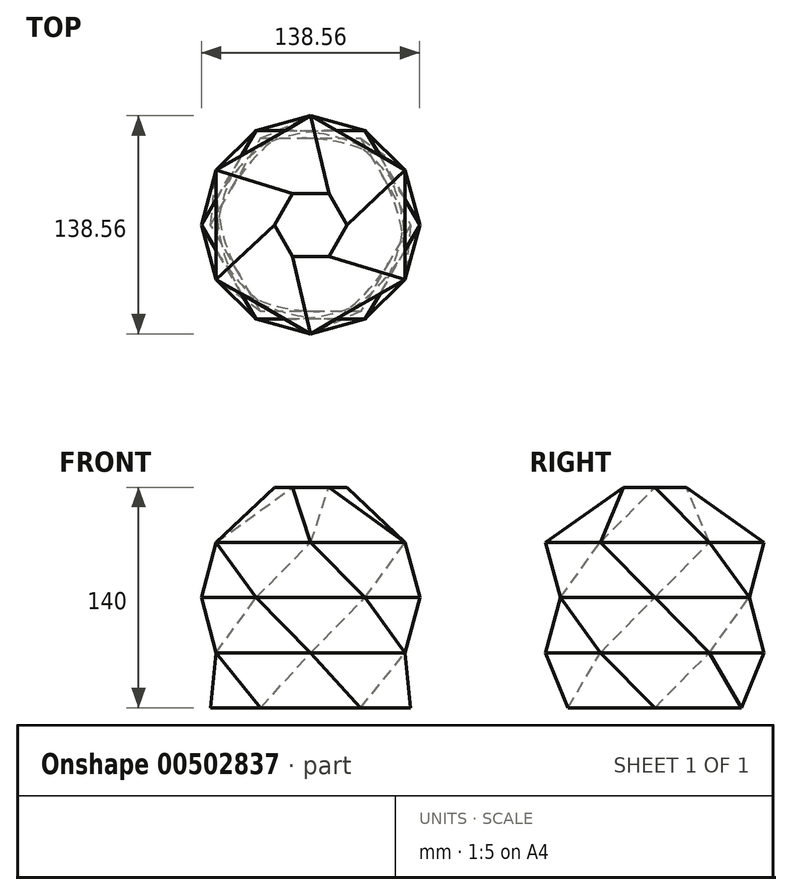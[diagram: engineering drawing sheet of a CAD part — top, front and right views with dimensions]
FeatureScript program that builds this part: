
annotation { "Feature Type Name" : "Feature", "Feature Type Description" : "" }
export const myFeature = defineFeature(function(context is Context, id is Id, definition is map)
    precondition{}
    {
        {
            var Q0;
            Q0=qCreatedBy(makeId("Top.planeOp"),FACE);
            cPlane(context, id + "F0", {"entities" : qUnion([Q0]), "cplaneType" : CPlaneType.OFFSET, "offset" : 35 * mm, "width" : 150 * mm, "height" : 150 * mm});
        }
        {
            var Q0;
            Q0=qCreatedBy(id+"F0.planeOp",FACE);
            cPlane(context, id + "F1", {"entities" : qUnion([Q0]), "cplaneType" : CPlaneType.OFFSET, "offset" : 35 * mm, "width" : 150 * mm, "height" : 150 * mm});
        }
        {
            var Q0;
            Q0=qCreatedBy(id+"F1.planeOp",FACE);
            cPlane(context, id + "F2", {"entities" : qUnion([Q0]), "cplaneType" : CPlaneType.OFFSET, "offset" : 35 * mm, "width" : 150 * mm, "height" : 150 * mm});
        }
        {
            var Q0;
            Q0=qCreatedBy(id+"F2.planeOp",FACE);
            cPlane(context, id + "F3", {"entities" : qUnion([Q0]), "cplaneType" : CPlaneType.OFFSET, "offset" : 35 * mm, "width" : 150 * mm, "height" : 150 * mm});
        }
        {
            var Q0;
            Q0=qCreatedBy(makeId("Top.planeOp"),FACE);
            var sketch = newSketch(context, id + "F4", { "sketchPlane" : qUnion([Q0])});
            skCircle(sketch, "E0.cCircle", {"center": v(0, 0) * mm, "radius": 55 * mm, "construction": true});
            skLineSegment(sketch, "E0.0", {"start": v(31.75, -55) * mm, "end": v(-31.75, -55) * mm});
            skLineSegment(sketch, "E0.1", {"start": v(-31.75, -55) * mm, "end": v(-63.5, 0) * mm});
            skLineSegment(sketch, "E0.2", {"start": v(-63.5, 0) * mm, "end": v(-31.75, 55) * mm});
            skLineSegment(sketch, "E0.3", {"start": v(-31.75, 55) * mm, "end": v(31.75, 55) * mm});
            skLineSegment(sketch, "E0.4", {"start": v(31.75, 55) * mm, "end": v(63.5, 0) * mm});
            skLineSegment(sketch, "E0.5", {"start": v(63.5, 0) * mm, "end": v(31.75, -55) * mm});
            skPoint(sketch, "E0.0.midPoint", {"position": v(0, -55) * mm});
            skSolve(sketch);
        }
        {
            var Q0;
            Q0=qCreatedBy(id+"F0.planeOp",FACE);
            var sketch = newSketch(context, id + "F5", { "sketchPlane" : qUnion([Q0])});
            skCircle(sketch, "E1.cCircle", {"center": v(0, 0) * mm, "radius": 60 * mm, "construction": true});
            skLineSegment(sketch, "E1.0", {"start": v(60, 34.64) * mm, "end": v(60, -34.64) * mm});
            skLineSegment(sketch, "E1.1", {"start": v(60, -34.64) * mm, "end": v(0, -69.28) * mm});
            skLineSegment(sketch, "E1.2", {"start": v(0, -69.28) * mm, "end": v(-60, -34.64) * mm});
            skLineSegment(sketch, "E1.3", {"start": v(-60, -34.64) * mm, "end": v(-60, 34.64) * mm});
            skLineSegment(sketch, "E1.4", {"start": v(-60, 34.64) * mm, "end": v(0, 69.28) * mm});
            skLineSegment(sketch, "E1.5", {"start": v(0, 69.28) * mm, "end": v(60, 34.64) * mm});
            skPoint(sketch, "E1.0.midPoint", {"position": v(60, 0) * mm});
            skSolve(sketch);
        }
        {
            var Q0;
            Q0=qCreatedBy(id+"F1.planeOp",FACE);
            var sketch = newSketch(context, id + "F6", { "sketchPlane" : qUnion([Q0])});
            skCircle(sketch, "E2.cCircle", {"center": v(0, 0) * mm, "radius": 60 * mm, "construction": true});
            skLineSegment(sketch, "E2.0", {"start": v(69.28, 0) * mm, "end": v(34.64, -60) * mm});
            skLineSegment(sketch, "E2.1", {"start": v(34.64, -60) * mm, "end": v(-34.64, -60) * mm});
            skLineSegment(sketch, "E2.2", {"start": v(-34.64, -60) * mm, "end": v(-69.28, 0) * mm});
            skLineSegment(sketch, "E2.3", {"start": v(-69.28, 0) * mm, "end": v(-34.64, 60) * mm});
            skLineSegment(sketch, "E2.4", {"start": v(-34.64, 60) * mm, "end": v(34.64, 60) * mm});
            skLineSegment(sketch, "E2.5", {"start": v(34.64, 60) * mm, "end": v(69.28, 0) * mm});
            skPoint(sketch, "E2.0.midPoint", {"position": v(51.96, -30) * mm});
            skSolve(sketch);
        }
        {
            var Q0;
            Q0=qCreatedBy(id+"F2.planeOp",FACE);
            var sketch = newSketch(context, id + "F7", { "sketchPlane" : qUnion([Q0])});
            skCircle(sketch, "E3.cCircle", {"center": v(0, 0) * mm, "radius": 60 * mm, "construction": true});
            skLineSegment(sketch, "E3.0", {"start": v(60, -34.64) * mm, "end": v(0, -69.28) * mm});
            skLineSegment(sketch, "E3.1", {"start": v(0, -69.28) * mm, "end": v(-60, -34.64) * mm});
            skLineSegment(sketch, "E3.2", {"start": v(-60, -34.64) * mm, "end": v(-60, 34.64) * mm});
            skLineSegment(sketch, "E3.3", {"start": v(-60, 34.64) * mm, "end": v(0, 69.28) * mm});
            skLineSegment(sketch, "E3.4", {"start": v(0, 69.28) * mm, "end": v(60, 34.64) * mm});
            skLineSegment(sketch, "E3.5", {"start": v(60, 34.64) * mm, "end": v(60, -34.64) * mm});
            skPoint(sketch, "E3.0.midPoint", {"position": v(30, -51.96) * mm});
            skSolve(sketch);
        }
        {
            var Q0;
            Q0=qCreatedBy(id+"F3.planeOp",FACE);
            var sketch = newSketch(context, id + "F8", { "sketchPlane" : qUnion([Q0])});
            skCircle(sketch, "E4.cCircle", {"center": v(0, 0) * mm, "radius": 20 * mm, "construction": true});
            skLineSegment(sketch, "E4.0", {"start": v(23.1, 0) * mm, "end": v(11.55, -20) * mm});
            skLineSegment(sketch, "E4.1", {"start": v(11.55, -20) * mm, "end": v(-11.55, -20) * mm});
            skLineSegment(sketch, "E4.2", {"start": v(-11.55, -20) * mm, "end": v(-23.1, 0) * mm});
            skLineSegment(sketch, "E4.3", {"start": v(-23.1, 0) * mm, "end": v(-11.55, 20) * mm});
            skLineSegment(sketch, "E4.4", {"start": v(-11.55, 20) * mm, "end": v(11.55, 20) * mm});
            skLineSegment(sketch, "E4.5", {"start": v(11.55, 20) * mm, "end": v(23.1, 0) * mm});
            skPoint(sketch, "E4.0.midPoint", {"position": v(17.32, -10) * mm});
            skSolve(sketch);
        }
        {
            var Q0;
            Q0=makeQuery(id+"F4.imprint","IMPRINT",FACE,{"disambiguationData":[TD([[makeQuery(id+"F4.imprint","IMPRINT",EDGE,{"derivedFrom":sQuery(id+"F4.wireOp",EDGE,"E0.0")}),-1.0]])]});
            var Q1;
            Q1=makeQuery(id+"F5.imprint","IMPRINT",FACE,{"disambiguationData":[TD([[makeQuery(id+"F5.imprint","IMPRINT",EDGE,{"derivedFrom":sQuery(id+"F5.wireOp",EDGE,"E1.0")}),-1.0]])]});
            var Q2;
            Q2=sQuery(id+"F4.wireOp",VERTEX,"E0.2.start");
            var Q3;
            Q3=sQuery(id+"F5.wireOp",VERTEX,"E1.4.start");
            loft(context, id + "F9", {"sheetProfilesArray" : [{ "sheetProfileEntities" : qUnion([Q0]) }, { "sheetProfileEntities" : qUnion([Q1]) }], "matchConnections" : true, "connections" : [{ "connectionEntities" : qUnion([Q2, Q3]), "connectionEdgeQueries" : qUnion([]), "connectionEdgeParameters" : [] }]});
        }
        {
            var Q1;
            Q1 = qSketchRegion(id + "F5", true);
            var Q2;
            Q2 = qSketchRegion(id + "F6", true);
            var Q3;
            Q3=sQuery(id+"F5.wireOp",VERTEX,"E1.3.start");
            var Q4;
            Q4=sQuery(id+"F6.wireOp",VERTEX,"E2.3.start");
            loft(context, id + "F10", {"operationType" : NewBodyOperationType.ADD, "sheetProfilesArray" : [{ "sheetProfileEntities" : qUnion([Q1]) }, { "sheetProfileEntities" : qUnion([Q2]) }], "matchConnections" : true, "connections" : [{ "connectionEntities" : qUnion([Q3, Q4]), "connectionEdgeQueries" : qUnion([]), "connectionEdgeParameters" : [] }]});
        }
        {
            var Q1;
            Q1 = qSketchRegion(id + "F6", true);
            var Q2;
            Q2 = qSketchRegion(id + "F7", true);
            var Q3;
            Q3=sQuery(id+"F6.wireOp",VERTEX,"E2.3.start");
            var Q4;
            Q4=sQuery(id+"F7.wireOp",VERTEX,"E3.3.start");
            loft(context, id + "F11", {"operationType" : NewBodyOperationType.ADD, "sheetProfilesArray" : [{ "sheetProfileEntities" : qUnion([Q1]) }, { "sheetProfileEntities" : qUnion([Q2]) }], "matchConnections" : true, "connections" : [{ "connectionEntities" : qUnion([Q3, Q4]), "connectionEdgeQueries" : qUnion([]), "connectionEdgeParameters" : [] }]});
        }
        {
            var Q1;
            Q1 = qSketchRegion(id + "F7", true);
            var Q2;
            Q2 = qSketchRegion(id + "F8", true);
            var Q3;
            Q3=sQuery(id+"F7.wireOp",VERTEX,"E3.2.start");
            var Q4;
            Q4=sQuery(id+"F8.wireOp",VERTEX,"E4.3.start");
            loft(context, id + "F12", {"operationType" : NewBodyOperationType.ADD, "sheetProfilesArray" : [{ "sheetProfileEntities" : qUnion([Q1]) }, { "sheetProfileEntities" : qUnion([Q2]) }], "matchConnections" : true, "connections" : [{ "connectionEntities" : qUnion([Q3, Q4]), "connectionEdgeQueries" : qUnion([]), "connectionEdgeParameters" : [] }]});
        }
    });
